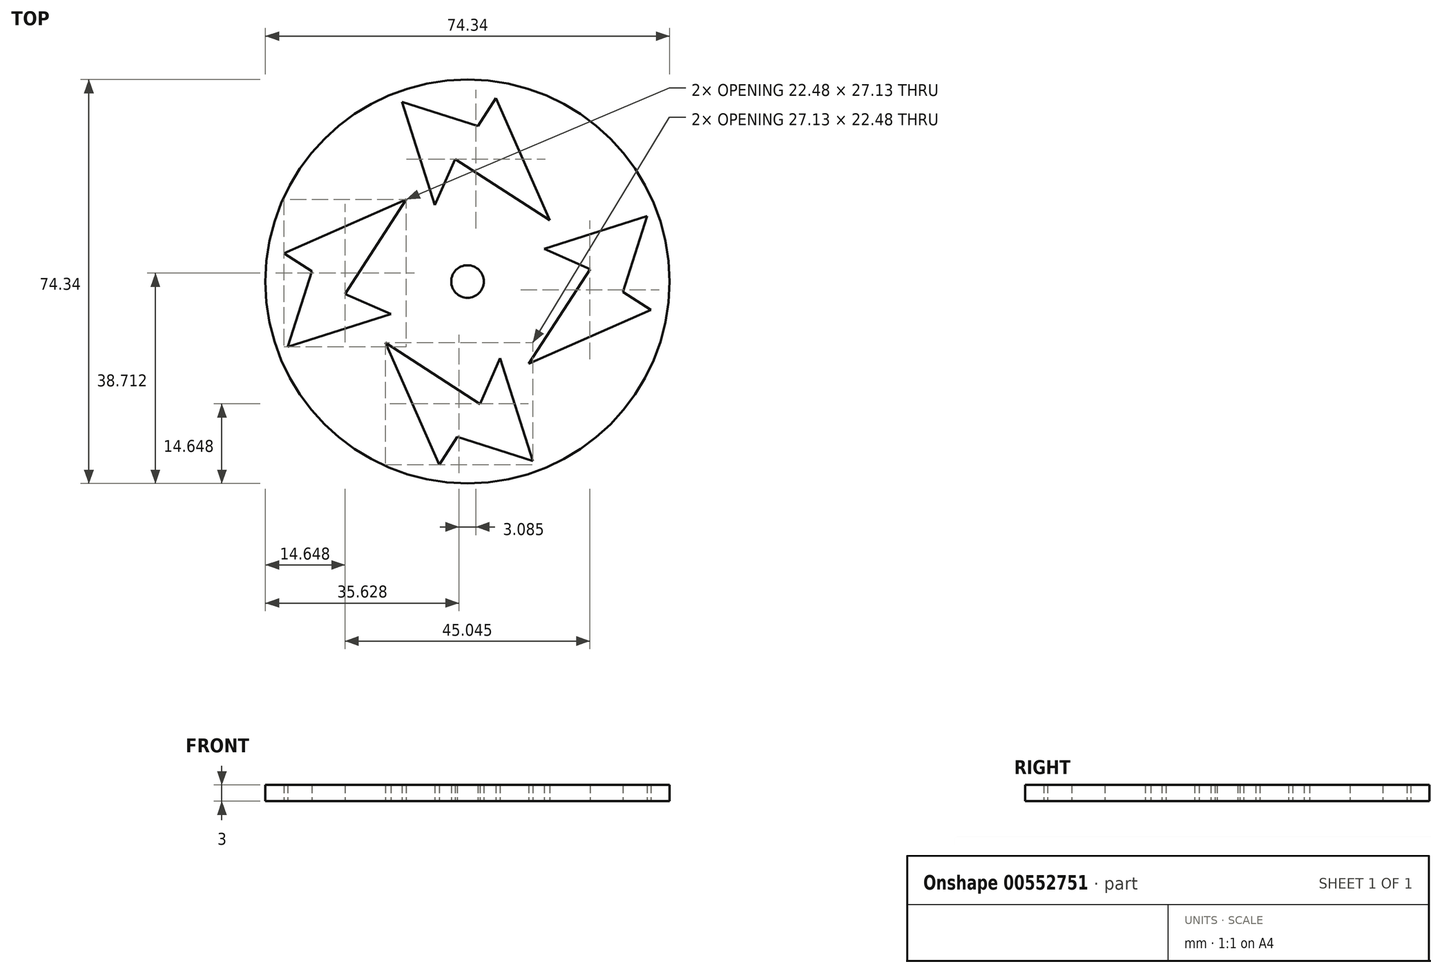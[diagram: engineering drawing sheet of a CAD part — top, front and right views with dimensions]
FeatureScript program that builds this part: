
annotation { "Feature Type Name" : "Feature", "Feature Type Description" : "" }
export const myFeature = defineFeature(function(context is Context, id is Id, definition is map)
    precondition{}
    {
        {
            var Q0;
            Q0=qCreatedBy(makeId("Top.planeOp"),FACE);
            var sketch = newSketch(context, id + "F0", { "sketchPlane" : qUnion([Q0])});
            skLineSegment(sketch, "E0.bottom", {"start": v(0, 0) * mm, "end": v(75, 0) * mm, "construction": true});
            skLineSegment(sketch, "E0.top", {"start": v(0, 75) * mm, "end": v(75, 75) * mm, "construction": true});
            skLineSegment(sketch, "E0.left", {"start": v(0, 0) * mm, "end": v(0, 75) * mm, "construction": true});
            skLineSegment(sketch, "E0.right", {"start": v(75, 0) * mm, "end": v(75, 75) * mm, "construction": true});
            skLineSegment(sketch, "E1", {"start": v(0, 75) * mm, "end": v(75, 0) * mm, "construction": true});
            skCircle(sketch, "E2", {"center": v(37.5, 37.5) * mm, "radius": 3 * mm});
            skCircle(sketch, "E3", {"center": v(37.5, 37.5) * mm, "radius": 37.17 * mm});
            skLineSegment(sketch, "E4.direction1", {"start": v(1.81, 27.12) * mm, "end": v(26.81, 27.12) * mm, "construction": true});
            skLineSegment(sketch, "E5.1.0", {"start": v(32.3, 3.74) * mm, "end": v(22.4, 26.22) * mm});
            skLineSegment(sketch, "E5.1.1", {"start": v(22.4, 26.22) * mm, "end": v(39.78, 14.95) * mm});
            skLineSegment(sketch, "E5.1.2", {"start": v(39.78, 14.95) * mm, "end": v(43.49, 23.42) * mm});
            skLineSegment(sketch, "E5.1.5", {"start": v(35.6, 8.9) * mm, "end": v(32.3, 3.74) * mm});
            skPoint(sketch, "E6.visualSharp", {"position": v(25.72, 49.28) * mm});
            skArc(sketch, "E6.filletArc", {"start": v(23.53, 47.08) * mm, "mid": v(23.55, 47.54) * mm, "end": v(23.1, 47.61) * mm});
            skLineSegment(sketch, "E7", {"start": v(35.6, 8.9) * mm, "end": v(49.52, 4.44) * mm});
            skLineSegment(sketch, "E8", {"start": v(49.52, 4.44) * mm, "end": v(43.49, 23.42) * mm});
            skLineSegment(sketch, "E9.1.0", {"start": v(48.78, 22.4) * mm, "end": v(60.05, 39.78) * mm});
            skLineSegment(sketch, "E9.1.1", {"start": v(60.05, 39.78) * mm, "end": v(51.58, 43.49) * mm});
            skLineSegment(sketch, "E9.1.2", {"start": v(70.56, 49.52) * mm, "end": v(51.58, 43.49) * mm});
            skLineSegment(sketch, "E9.1.3", {"start": v(66.1, 35.6) * mm, "end": v(70.56, 49.52) * mm});
            skLineSegment(sketch, "E9.1.4", {"start": v(66.1, 35.6) * mm, "end": v(71.26, 32.3) * mm});
            skLineSegment(sketch, "E9.1.5", {"start": v(71.26, 32.3) * mm, "end": v(48.78, 22.4) * mm});
            skLineSegment(sketch, "E9.2.0", {"start": v(52.6, 48.78) * mm, "end": v(35.22, 60.05) * mm});
            skLineSegment(sketch, "E9.2.1", {"start": v(35.22, 60.05) * mm, "end": v(31.51, 51.58) * mm});
            skLineSegment(sketch, "E9.2.2", {"start": v(25.48, 70.56) * mm, "end": v(31.51, 51.58) * mm});
            skLineSegment(sketch, "E9.2.3", {"start": v(39.4, 66.1) * mm, "end": v(25.48, 70.56) * mm});
            skLineSegment(sketch, "E9.2.4", {"start": v(39.4, 66.1) * mm, "end": v(42.7, 71.26) * mm});
            skLineSegment(sketch, "E9.2.5", {"start": v(42.7, 71.26) * mm, "end": v(52.6, 48.78) * mm});
            skLineSegment(sketch, "E9.3.0", {"start": v(26.22, 52.6) * mm, "end": v(14.95, 35.22) * mm});
            skLineSegment(sketch, "E9.3.1", {"start": v(14.95, 35.22) * mm, "end": v(23.42, 31.51) * mm});
            skLineSegment(sketch, "E9.3.2", {"start": v(4.44, 25.48) * mm, "end": v(23.42, 31.51) * mm});
            skLineSegment(sketch, "E9.3.3", {"start": v(8.9, 39.4) * mm, "end": v(4.44, 25.48) * mm});
            skLineSegment(sketch, "E9.3.4", {"start": v(8.9, 39.4) * mm, "end": v(3.74, 42.7) * mm});
            skLineSegment(sketch, "E9.3.5", {"start": v(3.74, 42.7) * mm, "end": v(26.22, 52.6) * mm});
            skSolve(sketch);
        }
        {
            var Q0;
            Q0=makeQuery(id+"F0.imprint","IMPRINT",FACE,{"disambiguationData":[TD([[makeQuery(id+"F0.imprint","IMPRINT",EDGE,{"derivedFrom":sQuery(id+"F0.wireOp",EDGE,"E2")}),-1.0]])]});
            extrude(context, id + "F1", {"entities" : qUnion([Q0]), "depth" : 3 * mm, "offsetDistance" : 25 * mm});
        }
    });
